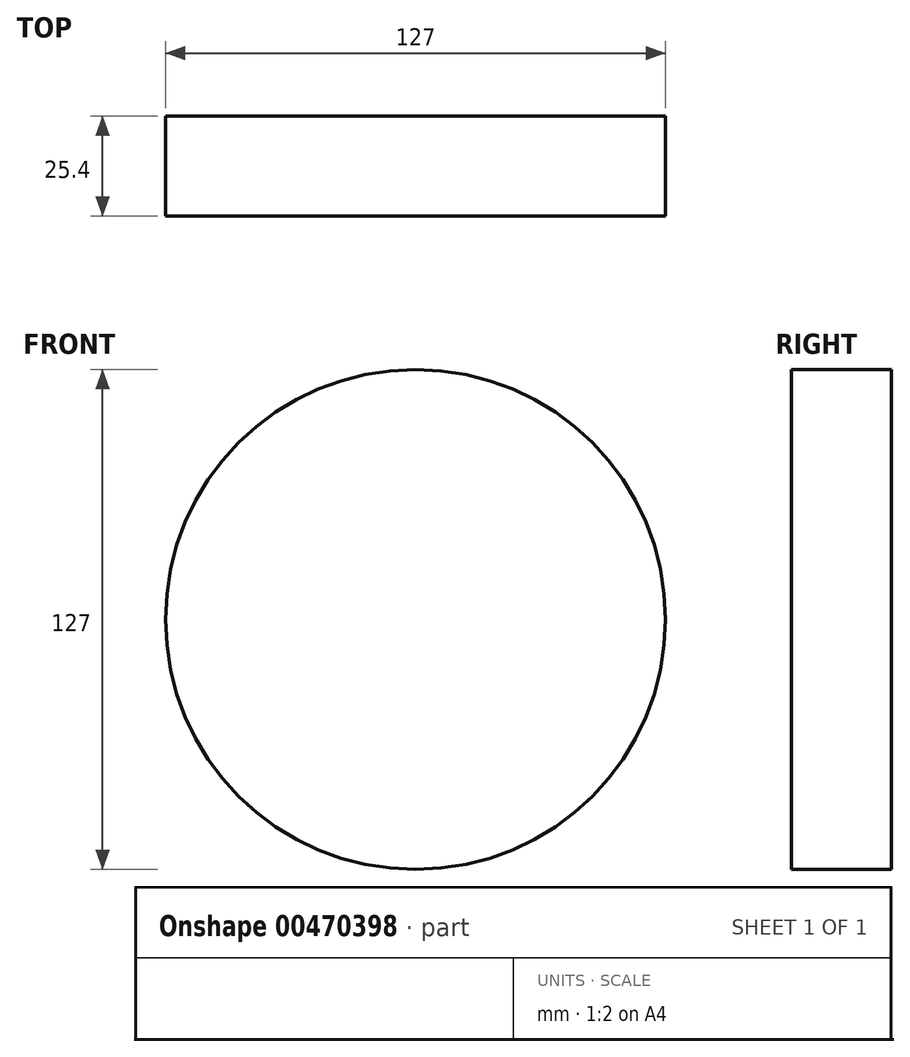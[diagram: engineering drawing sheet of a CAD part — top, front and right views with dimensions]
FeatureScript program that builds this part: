
annotation { "Feature Type Name" : "Feature", "Feature Type Description" : "" }
export const myFeature = defineFeature(function(context is Context, id is Id, definition is map)
    precondition{}
    {
        {
            var Q0;
            Q0=qCreatedBy(makeId("Front.planeOp"),FACE);
            var sketch = newSketch(context, id + "F0", { "sketchPlane" : qUnion([Q0])});
            skCircle(sketch, "E0", {"center": v(0, 0) * mm, "radius": 63.5 * mm});
            skArc(sketch, "E1", {"start": v(0, 63.5) * mm, "mid": v(-22.23, 31.75) * mm, "end": v(0, 0) * mm});
            skArc(sketch, "E2", {"start": v(0, 63.5) * mm, "mid": v(-12.7, 31.75) * mm, "end": v(0, 0) * mm});
            skSolve(sketch);
        }
        {
            var Q0;
            Q0=makeQuery(id+"F0.imprint","IMPRINT",FACE,{"disambiguationData":[TD([[makeQuery(id+"F0.imprint","IMPRINT",EDGE,{"derivedFrom":sQuery(id+"F0.wireOp",EDGE,"E1")}),1.0]])]});
            extrude(context, id + "F1", {"entities" : qUnion([Q0]), "depth" : 2.54 * mm});
        }
        {
            var Q0;
            Q0 = qSketchRegion(id + "F0", true);
            extrude(context, id + "F2", {"entities" : qUnion([Q0]), "operationType" : NewBodyOperationType.ADD, "depth" : 25.4 * mm});
        }
    });
